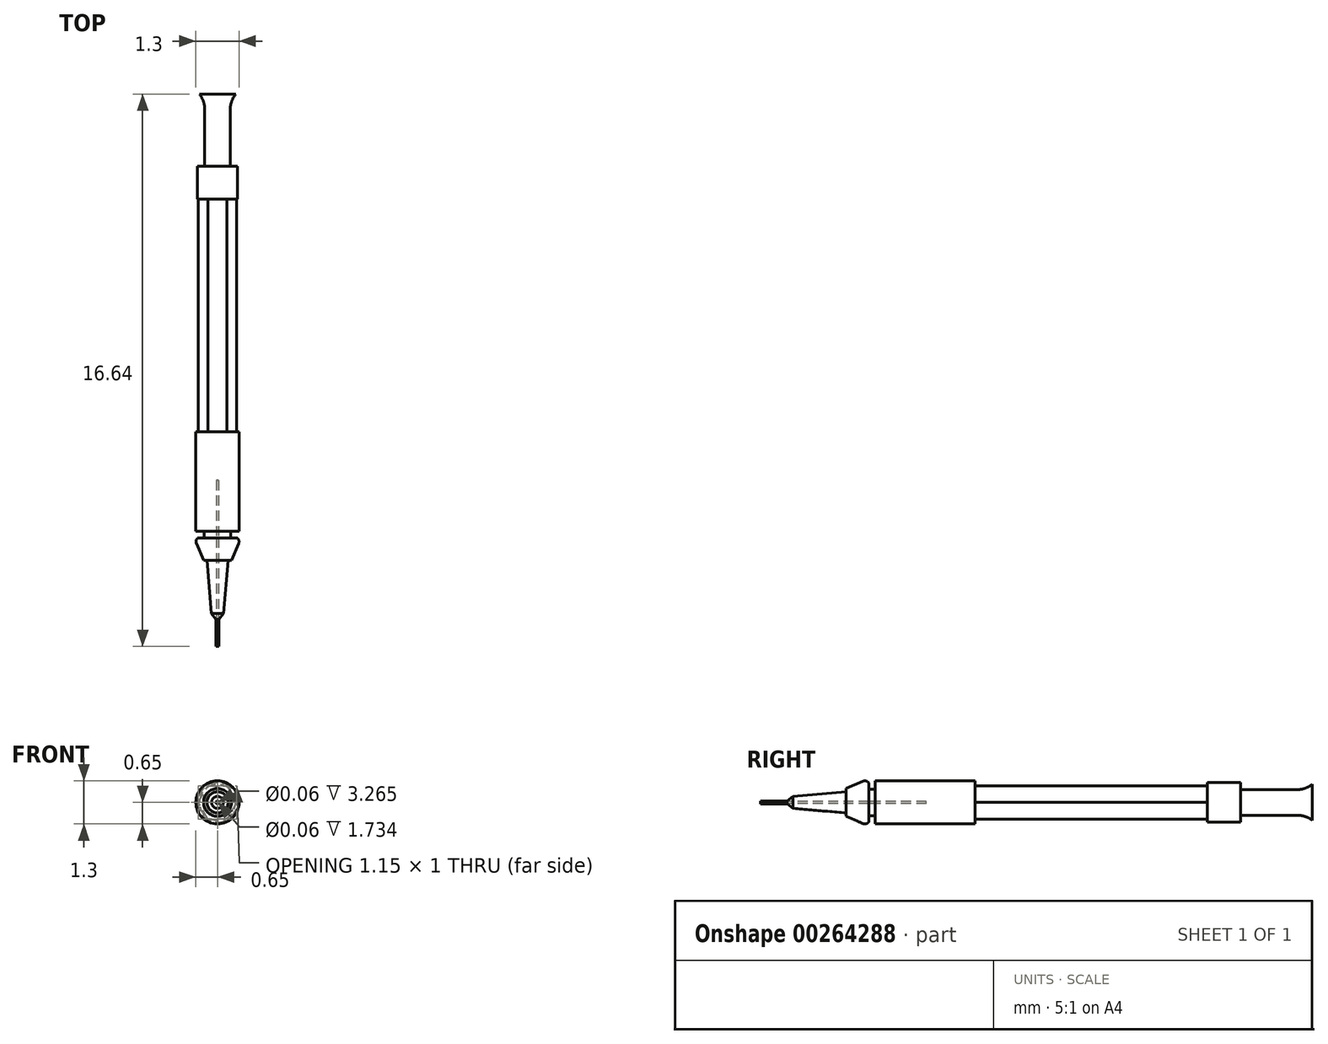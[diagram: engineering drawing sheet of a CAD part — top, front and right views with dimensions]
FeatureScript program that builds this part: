
annotation { "Feature Type Name" : "Feature", "Feature Type Description" : "" }
export const myFeature = defineFeature(function(context is Context, id is Id, definition is map)
    precondition{}
    {
        {
            var Q0;
            Q0=qCreatedBy(makeId("Front.planeOp"),FACE);
            var sketch = newSketch(context, id + "F0", { "sketchPlane" : qUnion([Q0])});
            skCircle(sketch, "E0.cCircle", {"center": v(0, 0) * mm, "radius": 0.5 * mm, "construction": true});
            skLineSegment(sketch, "E0.0", {"start": v(0.29, -0.5) * mm, "end": v(-0.29, -0.5) * mm});
            skLineSegment(sketch, "E0.1", {"start": v(-0.29, -0.5) * mm, "end": v(-0.58, 0) * mm});
            skLineSegment(sketch, "E0.2", {"start": v(-0.58, 0) * mm, "end": v(-0.29, 0.5) * mm});
            skLineSegment(sketch, "E0.3", {"start": v(-0.29, 0.5) * mm, "end": v(0.29, 0.5) * mm});
            skLineSegment(sketch, "E0.4", {"start": v(0.29, 0.5) * mm, "end": v(0.58, 0) * mm});
            skLineSegment(sketch, "E0.5", {"start": v(0.58, 0) * mm, "end": v(0.29, -0.5) * mm});
            skPoint(sketch, "E0.0.midPoint", {"position": v(0, -0.5) * mm});
            skSolve(sketch);
        }
        {
            var Q0;
            Q0=makeQuery(id+"F0.imprint","IMPRINT",FACE,{"disambiguationData":[TD([[makeQuery(id+"F0.imprint","IMPRINT",EDGE,{"derivedFrom":sQuery(id+"F0.wireOp",EDGE,"E0.0")}),-1.0]])]});
            extrude(context, id + "F1", {"entities" : qUnion([Q0]), "depth" : 8 * mm});
        }
        {
            var Q0;
            Q0=makeQuery(id+"F1.opExtrude","CAP_FACE",FACE,{"disambiguationData":[OSD([sQuery(id+"F0.wireOp",EDGE,"E0.0"),sQuery(id+"F0.wireOp",EDGE,"E0.1"),sQuery(id+"F0.wireOp",EDGE,"E0.2"),sQuery(id+"F0.wireOp",EDGE,"E0.3"),sQuery(id+"F0.wireOp",EDGE,"E0.4"),sQuery(id+"F0.wireOp",EDGE,"E0.5")])],"isStart":false});
            var sketch = newSketch(context, id + "F2", { "sketchPlane" : qUnion([Q0])});
            skCircle(sketch, "E1", {"center": v(0, 0) * mm, "radius": 0.65 * mm});
            skSolve(sketch);
        }
        {
            var Q0;
            Q0=makeQuery(id+"F2.imprint","IMPRINT",FACE,{"disambiguationData":[TD([[makeQuery(id+"F2.imprint","IMPRINT",EDGE,{"derivedFrom":sQuery(id+"F2.wireOp",EDGE,"E1")}),1.0]])]});
            var Q1;
            Q1=makeQuery(id+"F2.imprint","IMPRINT",FACE,{"disambiguationData":[TD([[makeQuery(id+"F2.imprint","IMPRINT",EDGE,{"derivedFrom":makeQuery(id+"F1.opExtrude","CAP_EDGE",EDGE,{"disambiguationData":[OSD([sQuery(id+"F0.wireOp",EDGE,"E0.0")])],"isStart":false})}),-1.0]])]});
            extrude(context, id + "F3", {"entities" : qUnion([Q0, Q1]), "operationType" : NewBodyOperationType.ADD, "depth" : 3 * mm});
        }
        {
            var Q0;
            Q0=makeQuery(id+"F3.opExtrude","CAP_FACE",FACE,{"disambiguationData":[OSD([sQuery(id+"F2.wireOp",EDGE,"E1")])],"isStart":false});
            var sketch = newSketch(context, id + "F4", { "sketchPlane" : qUnion([Q0])});
            skCircle(sketch, "E2", {"center": v(0, 0) * mm, "radius": 0.4 * mm});
            skSolve(sketch);
        }
        {
            var Q0;
            Q0=makeQuery(id+"F4.imprint","IMPRINT",FACE,{"disambiguationData":[TD([[makeQuery(id+"F4.imprint","IMPRINT",EDGE,{"derivedFrom":sQuery(id+"F4.wireOp",EDGE,"E2")}),1.0]])]});
            extrude(context, id + "F5", {"entities" : qUnion([Q0]), "operationType" : NewBodyOperationType.ADD, "depth" : 0.2 * mm});
        }
        {
            var Q0;
            Q0=qCreatedBy(makeId("Right.planeOp"),FACE);
            var sketch = newSketch(context, id + "F6", { "sketchPlane" : qUnion([Q0])});
            skLineSegment(sketch, "E3", {"start": v(-11.2, 0) * mm, "end": v(-12.76, 0) * mm, "construction": true});
            skLineSegment(sketch, "E4", {"start": v(-11.2, 0) * mm, "end": v(-11.2, 0.6) * mm});
            skArc(sketch, "E5", {"start": v(-11.2, 0.6) * mm, "mid": v(-11.28, 0.64) * mm, "end": v(-11.38, 0.64) * mm});
            skLineSegment(sketch, "E6", {"start": v(-11.38, 0.64) * mm, "end": v(-11.88, 0.42) * mm});
            skLineSegment(sketch, "E7", {"start": v(-11.88, 0.42) * mm, "end": v(-11.88, 0) * mm});
            skLineSegment(sketch, "E8", {"start": v(-11.88, 0) * mm, "end": v(-11.2, 0) * mm});
            skLineSegment(sketch, "E9", {"start": v(-12.76, 0) * mm, "end": v(-14.32, 0) * mm, "construction": true});
            skLineSegment(sketch, "E10", {"start": v(-14.32, 0) * mm, "end": v(-15.48, 0) * mm, "construction": true});
            skPoint(sketch, "E10.endSnap0", {"position": v(-13.54, 0) * mm});
            skLineSegment(sketch, "E11", {"start": v(-11.88, 0.32) * mm, "end": v(-13.48, 0.18) * mm});
            skLineSegment(sketch, "E12", {"start": v(-13.48, 0.18) * mm, "end": v(-13.7, 0) * mm});
            skLineSegment(sketch, "E13", {"start": v(-13.65, 0.04) * mm, "end": v(-14.47, 0.04) * mm});
            skLineSegment(sketch, "E14", {"start": v(-14.47, 0.04) * mm, "end": v(-14.47, 0) * mm});
            skLineSegment(sketch, "E15", {"start": v(-14.47, 0) * mm, "end": v(-11.88, 0) * mm});
            skSolve(sketch);
        }
        {
            var Q0;
            Q0=makeQuery(id+"F6.imprint","IMPRINT",FACE,{"disambiguationData":[TD([[makeQuery(id+"F6.imprint","IMPRINT",EDGE,{"derivedFrom":sQuery(id+"F6.wireOp",EDGE,"E4")}),1.0]])]});
            var Q1;
            {var subQ4=sQuery(id+"F6.wireOp",EDGE,"E11");Q1=makeQuery(id+"F6.imprint","IMPRINT",FACE,{"disambiguationData":[TD([[makeQuery(id+"F6.imprint","IMPRINT",EDGE,{"derivedFrom":subQ4}),1.0]])]});}
            var Q2;
            {var subQ3=sQuery(id+"F6.wireOp",EDGE,"E13");Q2=makeQuery(id+"F6.imprint","IMPRINT",FACE,{"disambiguationData":[TD([[makeQuery(id+"F6.imprint","IMPRINT",EDGE,{"derivedFrom":subQ3}),1.0]])]});}
            var Q3;
            Q3=sQuery(id+"F6.wireOp",EDGE,"E8");
            revolve(context, id + "F7", {"entities" : qUnion([Q0, Q1, Q2]), "axis" : qUnion([Q3]), "revolveType" : RevolveType.FULL});
        }
        {
            var Q0;
            Q0=qCreatedBy(makeId("Right.planeOp"),FACE);
            var sketch = newSketch(context, id + "F8", { "sketchPlane" : qUnion([Q0])});
            skLineSegment(sketch, "E16", {"start": v(0, 0) * mm, "end": v(4.42, 0) * mm, "construction": true});
            skLineSegment(sketch, "E17", {"start": v(0, 0.39) * mm, "end": v(1.72, 0.39) * mm});
            skArc(sketch, "E18", {"start": v(1.72, 0.39) * mm, "mid": v(1.96, 0.43) * mm, "end": v(2.17, 0.55) * mm});
            skLineSegment(sketch, "E19", {"start": v(2.17, 0.55) * mm, "end": v(2.17, 0) * mm});
            skLineSegment(sketch, "E20", {"start": v(0, 0) * mm, "end": v(2.17, 0) * mm});
            skLineSegment(sketch, "E21", {"start": v(0, 0.39) * mm, "end": v(0, 0) * mm});
            skSolve(sketch);
        }
        {
            var Q0;
            Q0=makeQuery(id+"F8.imprint","IMPRINT",FACE,{"disambiguationData":[TD([[makeQuery(id+"F8.imprint","IMPRINT",EDGE,{"derivedFrom":sQuery(id+"F8.wireOp",EDGE,"E17")}),-1.0]])]});
            var Q1;
            Q1=sQuery(id+"F8.wireOp",EDGE,"E20");
            revolve(context, id + "F9", {"operationType" : NewBodyOperationType.ADD, "entities" : qUnion([Q0]), "axis" : qUnion([Q1]), "revolveType" : RevolveType.FULL});
        }
        {
            var Q0;
            Q0=makeQuery(id+"F7.opRevolve","SWEPT_FACE",FACE,{"disambiguationData":[OSD([sQuery(id+"F6.wireOp",EDGE,"E14")])]});
            var sketch = newSketch(context, id + "F10", { "sketchPlane" : qUnion([Q0])});
            skCircle(sketch, "E22", {"center": v(0, 0) * mm, "radius": 0.03 * mm});
            skSolve(sketch);
        }
        {
            var Q0;
            Q0=makeQuery(id+"F10.imprint","IMPRINT",FACE,{"disambiguationData":[TD([[makeQuery(id+"F10.imprint","IMPRINT",EDGE,{"derivedFrom":sQuery(id+"F10.wireOp",EDGE,"E22")}),1.0]])]});
            extrude(context, id + "F11", {"entities" : qUnion([Q0]), "operationType" : NewBodyOperationType.REMOVE, "oppositeDirection" : true, "depth" : 5 * mm});
        }
        {
            var Q0;
            Q0=makeQuery(id+"F0.imprint","IMPRINT",FACE,{"disambiguationData":[TD([[makeQuery(id+"F0.imprint","IMPRINT",EDGE,{"derivedFrom":sQuery(id+"F0.wireOp",EDGE,"E0.0")}),-1.0]])]});
            var sketch = newSketch(context, id + "F12", { "sketchPlane" : qUnion([Q0])});
            skCircle(sketch, "E23", {"center": v(0, 0) * mm, "radius": 0.6 * mm});
            skSolve(sketch);
        }
        {
            var Q0;
            Q0=makeQuery(id+"F12.imprint","IMPRINT",FACE,{"disambiguationData":[TD([[makeQuery(id+"F12.imprint","IMPRINT",EDGE,{"derivedFrom":sQuery(id+"F12.wireOp",EDGE,"E23")}),1.0]])]});
            extrude(context, id + "F13", {"entities" : qUnion([Q0]), "operationType" : NewBodyOperationType.ADD, "depth" : 1 * mm});
        }
        {
            var Q0;
            Q0=qCreatedBy(makeId("Right.planeOp"),FACE);
            var sketch = newSketch(context, id + "F14", { "sketchPlane" : qUnion([Q0])});
            skFitSpline(sketch, "E24", {"points": [v(-1.18, 0.9) * mm, v(-0.97, 0.55) * mm, v(-1.01, 1.04) * mm, v(-4.64, 0.8) * mm, v(-4.57, 0.5) * mm, v(-3.95, 0.95) * mm, v(-1.18, 0.9) * mm]});
            skSolve(sketch);
        }
        {
            var Q0;
            Q0 = qConstructionFilter(qBodyType(qCreatedBy(id + "F14" ,EDGE), BodyType.WIRE), ConstructionObject.NO);
            extrude(context, id + "F15", {"bodyType" : ToolBodyType.SURFACE, "surfaceEntities" : qUnion([Q0]), "oppositeDirection" : true, "depth" : 0.25 * mm});
        }
        {
            var Q0;
            Q0 = qConstructionFilter(qBodyType(qCreatedBy(id + "F14" ,EDGE), BodyType.WIRE), ConstructionObject.NO);
            extrude(context, id + "F16", {"bodyType" : ToolBodyType.SURFACE, "surfaceEntities" : qUnion([Q0]), "depth" : 0.25 * mm});
        }
    });
